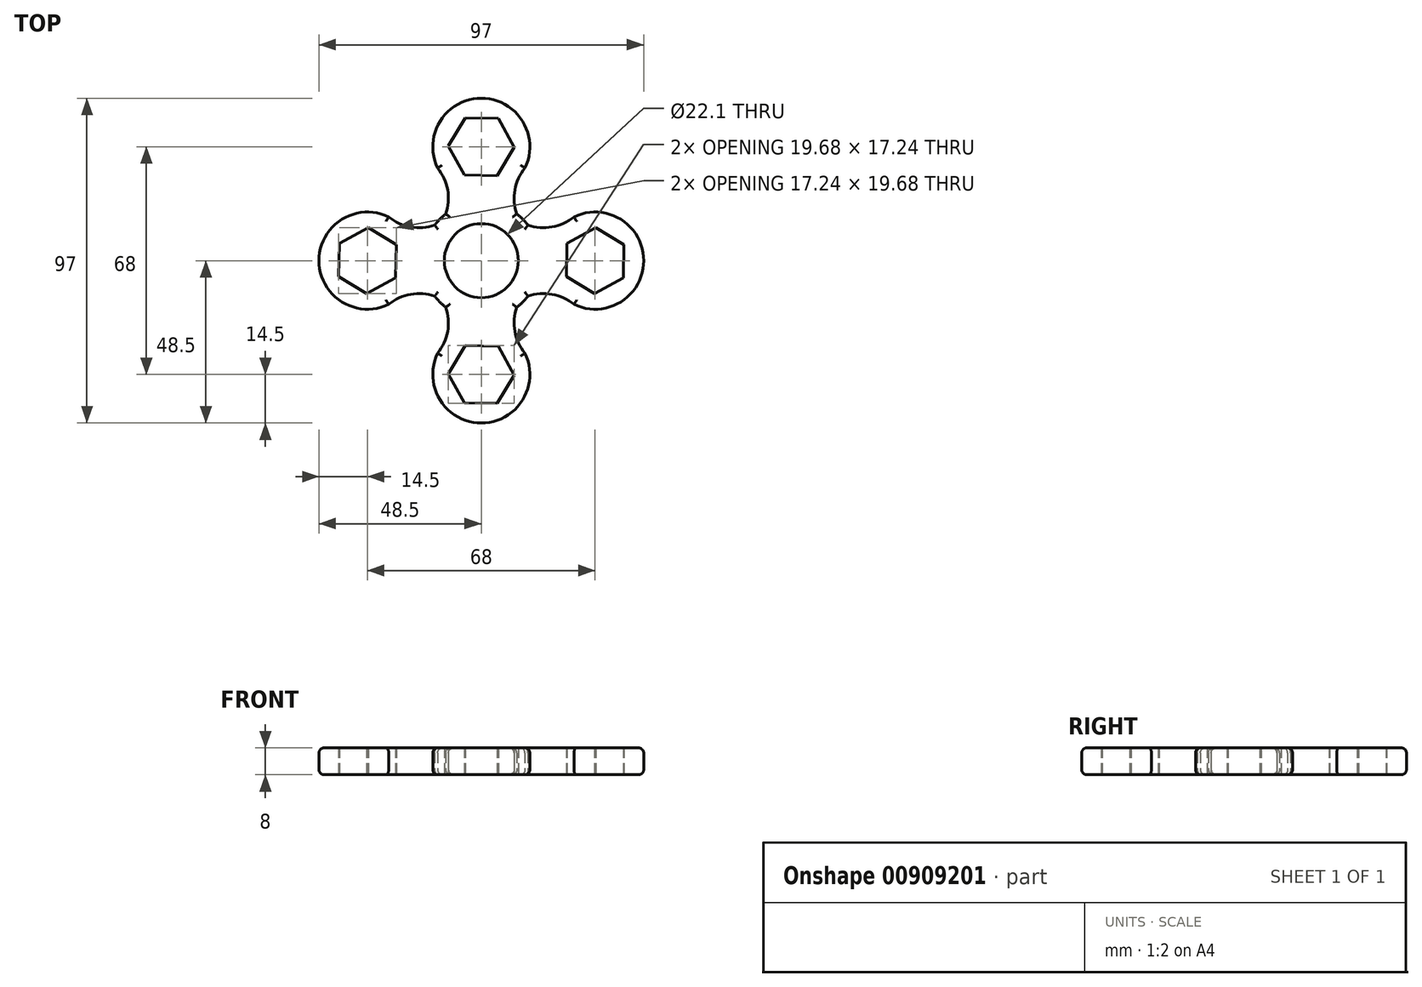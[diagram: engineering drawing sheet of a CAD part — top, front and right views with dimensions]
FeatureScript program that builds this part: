
annotation { "Feature Type Name" : "Feature", "Feature Type Description" : "" }
export const myFeature = defineFeature(function(context is Context, id is Id, definition is map)
    precondition{}
    {
        {
            var Q0;
            Q0=qCreatedBy(makeId("Top.planeOp"),FACE);
            var sketch = newSketch(context, id + "F0", { "sketchPlane" : qUnion([Q0])});
            skCircle(sketch, "E0", {"center": v(0, 0) * mm, "radius": 11.05 * mm});
            skLineSegment(sketch, "E1", {"start": v(0, 34) * mm, "end": v(0, 0) * mm, "construction": true});
            skCircle(sketch, "E2.cCircle", {"center": v(0, 34) * mm, "radius": 8.53 * mm});
            skLineSegment(sketch, "E2.0", {"start": v(9.84, 33.8) * mm, "end": v(4.75, 25.38) * mm});
            skLineSegment(sketch, "E2.1", {"start": v(4.75, 25.38) * mm, "end": v(-5.1, 25.58) * mm});
            skLineSegment(sketch, "E2.2", {"start": v(-5.1, 25.58) * mm, "end": v(-9.84, 34.2) * mm});
            skLineSegment(sketch, "E2.3", {"start": v(-9.84, 34.2) * mm, "end": v(-4.75, 42.62) * mm});
            skLineSegment(sketch, "E2.4", {"start": v(-4.75, 42.62) * mm, "end": v(5.1, 42.42) * mm});
            skLineSegment(sketch, "E2.5", {"start": v(5.1, 42.42) * mm, "end": v(9.84, 33.8) * mm});
            skPoint(sketch, "E2.0.midPoint", {"position": v(7.3, 29.59) * mm});
            skCircle(sketch, "E3", {"center": v(0, 0) * mm, "radius": 0.5 * mm});
            skCircle(sketch, "E4", {"center": v(0, 0) * mm, "radius": 17.5 * mm});
            skPoint(sketch, "E5.startSnap0", {"position": v(-7.47, 29.89) * mm});
            skCircle(sketch, "E6", {"center": v(0, 34) * mm, "radius": 14.5 * mm});
            skArc(sketch, "E7", {"start": v(-10.6, 13.92) * mm, "mid": v(-10.04, 21.1) * mm, "end": v(-13.04, 27.66) * mm});
            skArc(sketch, "E8.MirrorCS", {"start": v(10.6, 13.92) * mm, "mid": v(10.04, 21.1) * mm, "end": v(13.04, 27.66) * mm});
            skSolve(sketch);
        }
        {
            var Q0;
            {var subQ0=sQuery(id+"F0.wireOp",EDGE,"E2.5");var subQ13=sQuery(id+"F0.wireOp",EDGE,"E2.0");var subQ14=makeQuery(id+"F0.imprint","INTERSECT",VERTEX,{"derivedFrom":[subQ13,subQ0]});Q0=makeQuery(id+"F0.imprint","IMPRINT",FACE,{"disambiguationData":[TD([[makeQuery(id+"F0.imprint","IMPRINT",EDGE,{"disambiguationData":[TD([[subQ14,-1.0]])],"derivedFrom":subQ13}),1.0]])]});}
            var Q1;
            {var subQ0=sQuery(id+"F0.wireOp",EDGE,"E7");var subQ1=sQuery(id+"F0.wireOp",EDGE,"E4");var subQ2=makeQuery(id+"F0.imprint","INTERSECT",VERTEX,{"derivedFrom":[subQ1,subQ0]});Q1=makeQuery(id+"F0.imprint","IMPRINT",FACE,{"disambiguationData":[TD([[makeQuery(id+"F0.imprint","IMPRINT",EDGE,{"disambiguationData":[TD([[subQ2,1.0]])],"derivedFrom":subQ1}),-1.0]])]});}
            var Q2;
            Q2=makeQuery(id+"F0.imprint","IMPRINT",FACE,{"disambiguationData":[TD([[makeQuery(id+"F0.imprint","IMPRINT",EDGE,{"derivedFrom":sQuery(id+"F0.wireOp",EDGE,"E0")}),-1.0]])]});
            extrude(context, id + "F1", {"entities" : qUnion([Q0, Q1, Q2]), "depth" : 8 * mm, "offsetDistance" : 25 * mm});
        }
        {
            var Q0;
            Q0=makeQuery(id+"F1.opExtrude","CAP_EDGE",EDGE,{"disambiguationData":[OSD([sQuery(id+"F0.wireOp",EDGE,"E6")])],"isStart":false});
            var Q1;
            Q1=makeQuery(id+"F1.opExtrude","CAP_EDGE",EDGE,{"disambiguationData":[OSD([sQuery(id+"F0.wireOp",EDGE,"E8.MirrorCS")])],"isStart":false});
            var Q2;
            Q2=makeQuery(id+"F1.opExtrude","CAP_EDGE",EDGE,{"disambiguationData":[OSD([sQuery(id+"F0.wireOp",EDGE,"E4")])],"isStart":false});
            var Q3;
            Q3=makeQuery(id+"F1.opExtrude","CAP_EDGE",EDGE,{"disambiguationData":[OSD([sQuery(id+"F0.wireOp",EDGE,"E7")])],"isStart":false});
            var Q4;
            Q4=makeQuery(id+"F1.opExtrude","CAP_EDGE",EDGE,{"disambiguationData":[OSD([sQuery(id+"F0.wireOp",EDGE,"E4")])],"isStart":true});
            var Q5;
            Q5=makeQuery(id+"F1.opExtrude","CAP_EDGE",EDGE,{"disambiguationData":[OSD([sQuery(id+"F0.wireOp",EDGE,"E8.MirrorCS")])],"isStart":true});
            var Q6;
            Q6=makeQuery(id+"F1.opExtrude","CAP_EDGE",EDGE,{"disambiguationData":[OSD([sQuery(id+"F0.wireOp",EDGE,"E6")])],"isStart":true});
            var Q7;
            Q7=makeQuery(id+"F1.opExtrude","CAP_EDGE",EDGE,{"disambiguationData":[OSD([sQuery(id+"F0.wireOp",EDGE,"E7")])],"isStart":true});
            fillet(context, id + "F2", {"entities" : qUnion([Q0, Q1, Q2, Q3, Q4, Q5, Q6, Q7]), "radius" : 1.5 * mm, "tangentPropagation" : true, "allowEdgeOverflow" : false});
        }
        {
            var Q0;
            Q0=makeQuery(id+"F1.opExtrude","SWEPT_BODY",BODY,{"disambiguationData":[OSD([sQuery(id+"F0.wireOp",EDGE,"E0"),sQuery(id+"F0.wireOp",EDGE,"E2.0"),sQuery(id+"F0.wireOp",EDGE,"E2.1"),sQuery(id+"F0.wireOp",EDGE,"E2.2"),sQuery(id+"F0.wireOp",EDGE,"E2.3"),sQuery(id+"F0.wireOp",EDGE,"E2.4"),sQuery(id+"F0.wireOp",EDGE,"E2.5"),sQuery(id+"F0.wireOp",EDGE,"E4"),sQuery(id+"F0.wireOp",EDGE,"E6"),sQuery(id+"F0.wireOp",EDGE,"E7"),sQuery(id+"F0.wireOp",EDGE,"E8.MirrorCS")])]});
            var Q1;
            Q1=makeQuery(id+"F1.opExtrude","CAP_EDGE",EDGE,{"disambiguationData":[OSD([sQuery(id+"F0.wireOp",EDGE,"E0")])],"isStart":true});
            circularPattern(context, id + "F3", {"operationType" : NewBodyOperationType.ADD, "entities" : qUnion([Q0]), "axis" : qUnion([Q1]), "angle" : 360 * degree, "instanceCount" : 4, "equalSpace" : true});
        }
    });
